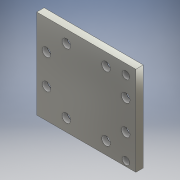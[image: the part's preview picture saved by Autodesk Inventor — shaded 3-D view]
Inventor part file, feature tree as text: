
AUTODESK INVENTOR PART (.ipt)
format: ipt  version: 2017 (Build 210142000, 142)  size: 215,040 bytes
history: native  units: mm
features: extrude x3, sketch x2, projected_geometry x1
ambient origin geometry x8: Origin, YZ Plane, XZ Plane, XY Plane, X Axis, Y Axis, Z Axis, Center Point
bodies: Solid1 (feature_tree)
feature tree (6):
  extrude  "Extrusion1"  Depth=3.0mm TaperAngle=0.0deg
  extrude  "Extrusion2"  Depth=3.0mm TaperAngle=0.0deg
  extrude  "Extrusion4"  Depth=3.0mm
  sketch  "Sketch2"  dims[d0=40.0mm d1=36.0mm d2=3.0mm d3=0.0mm]
  sketch  "Sketch5"  dims[d4=4.0mm d5=12.0mm d6=12.0mm d7=6.0mm d8=6.0mm d9=3.0mm d10=0.0mm d11=6.0mm d13=0.0mm d14=0.0mm d15=5.0mm d16=4.0mm d17=4.0mm d18=12.0mm d19=4.0mm d20=24.0mm d21=12.0mm d22=5.0mm d23=12.0mm d24=31.0mm d25=28.0mm d26=5.0mm d27=28.0mm d29=36.0mm d30=36.0mm d31=4.0mm d32=36.0mm d34=4.0mm d35=0.0mm d36=35.939652mm d37=4.060348mm d38=35.939652mm d39=3.5mm d40=0.0mm d41=0.0mm d42=3.5mm d43=0.0mm d44=0.0mm d45=6.0mm d46=3.5mm d47=0.0mm d48=0.0mm d49=6.0mm d50=3.5mm d51=0.0mm d52=0.0mm d53=6.0mm d54=3.5mm d55=0.0mm d56=0.0mm d57=6.0mm d58=3.5mm d59=0.0mm d60=0.0mm d61=6.0mm d62=3.5mm d63=0.0mm d64=0.0mm d65=6.0mm d66=3.5mm d67=0.0mm d68=0.0mm d69=6.0mm d72=2.0mm d73=0.0mm d74=68.0mm d75=67.0mm d76=68.0mm d77=67.0mm d78=68.0mm d79=67.0mm d80=75.939652mm d81=60.0mm d88=30.0mm d89=3.0mm]
  projected_geometry  "Projected Loop1"
